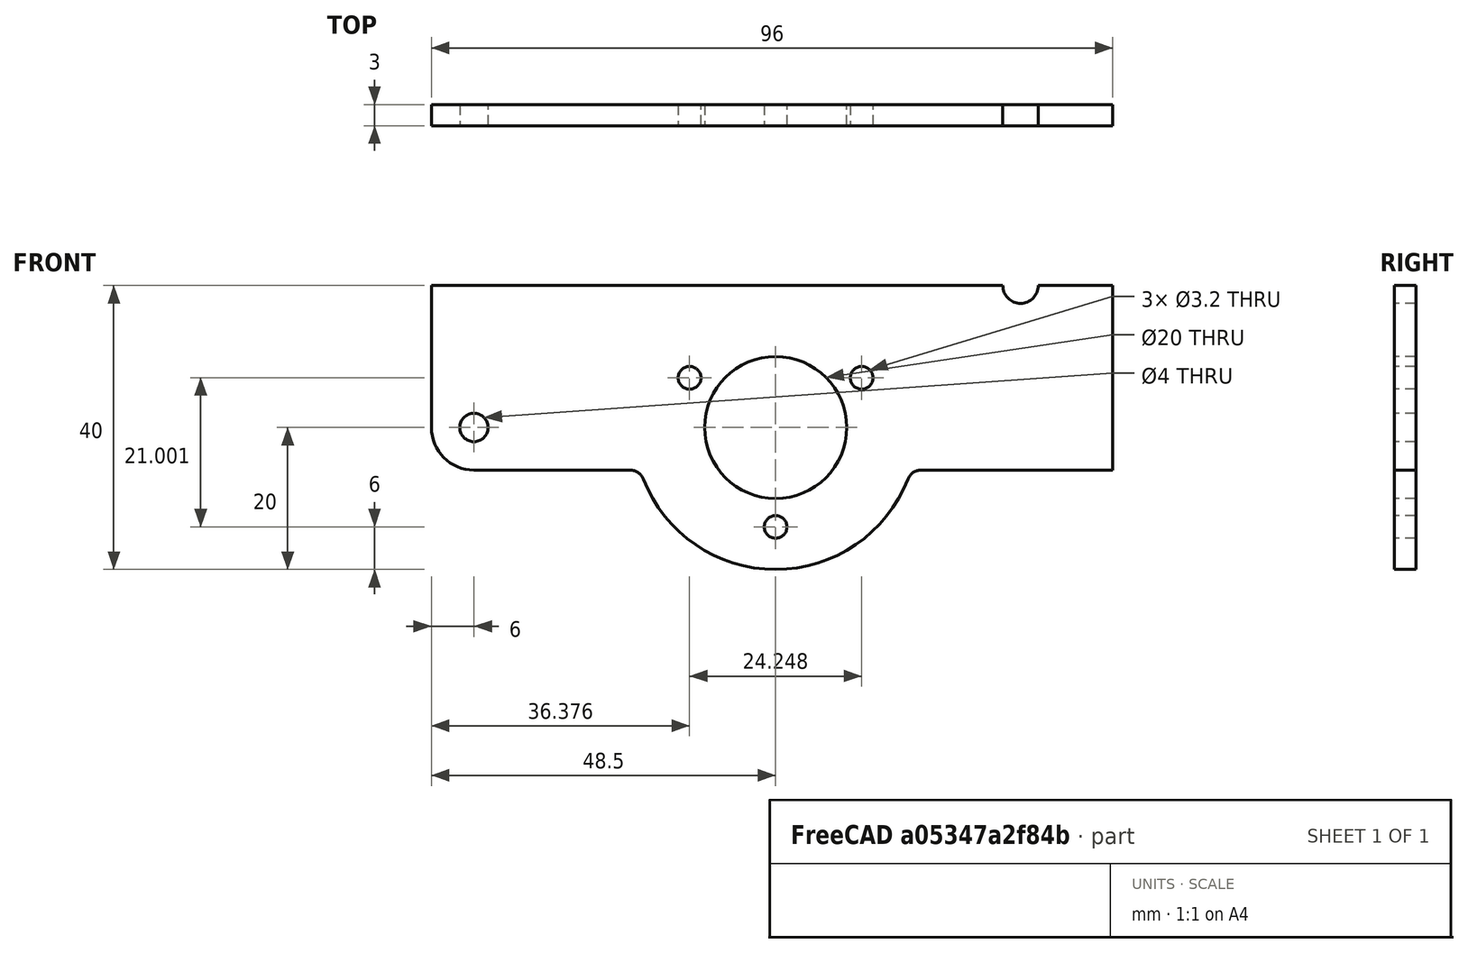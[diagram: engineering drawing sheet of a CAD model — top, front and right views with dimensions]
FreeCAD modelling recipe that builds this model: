
FCSTD DOCUMENT  (FreeCAD 0.15R4669 (Git))
Label: BR_supportCodeur
License: All rights reserved
LicenseURL: http://en.wikipedia.org/wiki/All_rights_reserved
objects: Sketcher::SketchObject×1, Part::Extrusion×1
note: 2 computed .brp shape members not serialized (recipe doc carries the construction recipe); baked Part::Feature solids carry a one-line shape summary decoded from their .brp

FEATURE [Sketcher::SketchObject] Sketch  label="sketchSupportCodeur"
  Placement = pos=(0,0,0) rot=(1,0,0;1.5708rad)
  sketch-geometry (16):
    g0: Circle CenterX=-42.5 CenterY=0 CenterZ=0 NormalX=0 NormalY=0 NormalZ=1 Radius=2
    g1: ArcOfCircle CenterX=-42.5 CenterY=0 CenterZ=0 NormalX=0 NormalY=0 NormalZ=1 Radius=6 StartAngle=3.14159 EndAngle=4.71239
    g2: Circle CenterX=0 CenterY=0 CenterZ=0 NormalX=0 NormalY=0 NormalZ=1 Radius=10
    g3: ArcOfCircle CenterX=0 CenterY=0 CenterZ=0 NormalX=0 NormalY=0 NormalZ=1 Radius=20 StartAngle=3.51376 EndAngle=5.91102
    g4: ArcOfCircle CenterX=34.5 CenterY=20 CenterZ=0 NormalX=0 NormalY=0 NormalZ=1 Radius=2.5 StartAngle=3.14159 EndAngle=6.28319
    g5: LineSegment StartX=47.5 StartY=-6 StartZ=0 EndX=47.5 EndY=20 EndZ=0
    g6: LineSegment StartX=47.5 StartY=20 StartZ=0 EndX=37 EndY=20 EndZ=0
    g7: Circle CenterX=-12.124 CenterY=7.00062 CenterZ=0 NormalX=0 NormalY=0 NormalZ=1 Radius=1.6
    g8: Circle CenterX=0 CenterY=-14 CenterZ=0 NormalX=0 NormalY=0 NormalZ=1 Radius=1.6
    g9: Circle CenterX=12.124 CenterY=7.00062 CenterZ=0 NormalX=0 NormalY=0 NormalZ=1 Radius=1.6
    g10: ArcOfCircle CenterX=-20.4939 CenterY=-8 CenterZ=0 NormalX=0 NormalY=0 NormalZ=1 Radius=2 StartAngle=0.372169 EndAngle=1.5708
    g11: LineSegment StartX=-42.5 StartY=-6 StartZ=0 EndX=-20.4939 EndY=-6 EndZ=0
    g12: LineSegment StartX=47.5 StartY=-6 StartZ=0 EndX=20.4939 EndY=-6 EndZ=0
    g13: ArcOfCircle CenterX=20.4939 CenterY=-8 CenterZ=0 NormalX=0 NormalY=0 NormalZ=1 Radius=2 StartAngle=1.5708 EndAngle=2.76942
    g14: LineSegment StartX=-48.5 StartY=20 StartZ=0 EndX=32 EndY=20 EndZ=0
    g15: LineSegment StartX=-48.5 StartY=20 StartZ=0 EndX=-48.5 EndY=-1.46637e-07 EndZ=0
  constraints (49):
    c: PointOnObject(g0,g-1)
    c: Coincident(g1,g0)
    c: Coincident(g2,g-1)
    c: Vertical(g5)
    c: Coincident(g6,g5)
    c: Coincident(g6,g4)
    c: Radius(g0) = 2
    c: Radius(g2) = 10
    c: Radius(g4) = 2.5
    c: Radius(g1) = 6
    c: DistanceX(g4,g5) = 13
    c: DistanceX(g-1,g0) = -42.5
    c: Coincident(g-1,g3)
    c: DistanceX(g-1,g5) = 47.5
    c: PointOnObject(g8,g-2)
    c: DistanceY(g-1,g8) = -14
    c: Distance(g-1,g7) = 14
    c: Symmetric(g7,g9,g-2)
    c: Equal(g8,g7)
    c: Equal(g8,g9)
    c: Radius(g9) = 1.6
    c: DistanceX(g-1,g9) = 12.124
    c: Radius(g3) = 20
    c: Coincident(g11,g1)
    c: Horizontal(g11)
    c: Coincident(g11,g10)
    c: Coincident(g10,g3)
    c: Radius(g10) = 2
    c: Tangent(g11,g10)
    c: Tangent(g3,g10)
    c: Coincident(g12,g5)
    c: Horizontal(g12)
    c: Coincident(g12,g13)
    c: Coincident(g3,g13)
    c: Radius(g13) = 2
    c: Tangent(g3,g13)
    c: Tangent(g12,g13)
    c: Tangent(g1,g11)
    c: PointOnObject(g12,g11)
    c: Horizontal(g14)
    c: Vertical(g15)
    c: Coincident(g15,g1)
    c: Coincident(g15,g14)
    c: DistanceY(g-1,g14) = 20
    c: Tangent(g1,g15)
    c: Horizontal(g6)
    c: Coincident(g14,g4)
    c: PointOnObject(g4,g14)
    c: PointOnObject(g4,g14)
FEATURE [Part::Extrusion] Extrude001  label="supportCodeur"
  Base = -> Sketch
  Dir = (0,3,0)
  Solid = true
